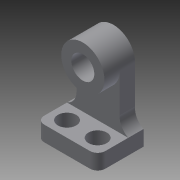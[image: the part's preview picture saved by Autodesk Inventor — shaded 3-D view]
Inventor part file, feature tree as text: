
AUTODESK INVENTOR PART (.ipt)
format: ipt  version: 2015 (Build 190159000, 159)  size: 131,072 bytes
history: native  units: in
note: dims shown in document units (in); Inventor stores cm internally (conversion verified against a paired STEP export)
features: extrude x5, sketch x4, fillet x1, hole x1
ambient origin geometry x8: Origin, YZ Plane, XZ Plane, XY Plane, X Axis, Y Axis, Z Axis, Center Point
bodies: Solid1 (feature_tree)
feature tree (11):
  extrude  "Extrusion1"  Depth=1.5in
  fillet  "Fillet1"  Radius=0.5in
  sketch  "Sketch2"  dims[d4=0.25in d16=0.5in]
  extrude  "Extrusion2"  Depth=0.5in
  sketch  "Sketch4"  dims[d43=1.0in d44=0.0in d45=0.5in d46=0.0in d47=0.6in d48=0.75in d49=0.375in d50=0.25in d51=0.5635in d52=1.0in d53=0.8108in]
  extrude  "Extrusion3"  Depth=1.0in TaperAngle=0.0deg
  extrude  "Extrusion4"  Depth=0.5in TaperAngle=0.0deg
  extrude  "Extrusion5"  [1 undecoded]
  hole  "Hole2"  [1 undecoded]
  sketch  "Sketch1"  dims[d0=2.0in d1=1.5in d2=0.5in d3=0.0in]
  sketch  "Sketch3"  dims[d17=2.5in d18=0.0in d41=1.0in d42=0.0in]
note: 2 required parameter values undecoded (feature->parameter linkage not recoverable at this tier; creation-order binding heuristic only, values carry confidence <= 0.55)
